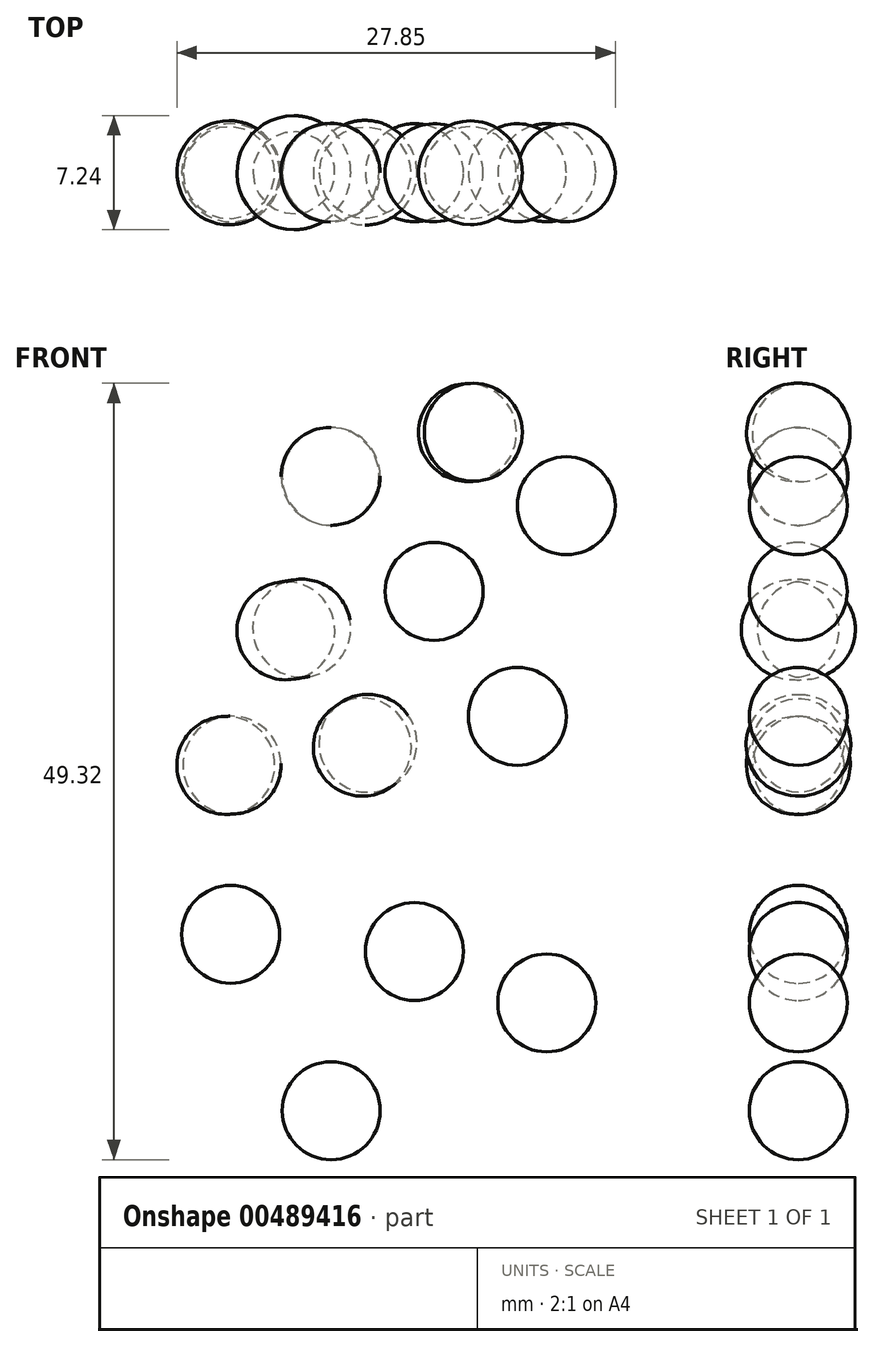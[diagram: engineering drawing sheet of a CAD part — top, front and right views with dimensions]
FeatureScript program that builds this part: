
annotation { "Feature Type Name" : "Feature", "Feature Type Description" : "" }
export const myFeature = defineFeature(function(context is Context, id is Id, definition is map)
    precondition{}
    {
        {
            var Q0;
            Q0=qCreatedBy(makeId("Front.planeOp"),FACE);
            var sketch = newSketch(context, id + "F0", { "sketchPlane" : qUnion([Q0])});
            skCircle(sketch, "E0", {"center": v(-19.54, 6.69) * mm, "radius": 3.11 * mm});
            skCircle(sketch, "E1", {"center": v(-10.05, 8.4) * mm, "radius": 3.11 * mm});
            skCircle(sketch, "E2", {"center": v(-16.58, -6.54) * mm, "radius": 3.11 * mm});
            skCircle(sketch, "E3", {"center": v(-15.34, 16.33) * mm, "radius": 3.11 * mm});
            skCircle(sketch, "E4", {"center": v(-12.85, 26.45) * mm, "radius": 3.11 * mm});
            skCircle(sketch, "E5", {"center": v(-6.94, 21.78) * mm, "radius": 3.11 * mm});
            skCircle(sketch, "E6", {"center": v(-21.87, 23.64) * mm, "radius": 3.11 * mm});
            skCircle(sketch, "E7", {"center": v(-23.74, 14) * mm, "radius": 3.11 * mm});
            skCircle(sketch, "E8", {"center": v(-28.56, 5.29) * mm, "radius": 3.11 * mm});
            skCircle(sketch, "E9", {"center": v(-28.25, -5.45) * mm, "radius": 3.11 * mm});
            skCircle(sketch, "E10", {"center": v(-21.87, -16.65) * mm, "radius": 3.11 * mm});
            skCircle(sketch, "E11", {"center": v(-8.18, -9.8) * mm, "radius": 3.11 * mm});
            skLineSegment(sketch, "E12", {"start": v(-21.95, 30.73) * mm, "end": v(-21.87, 18.16) * mm});
            skLineSegment(sketch, "E13", {"start": v(-24.94, 18.16) * mm, "end": v(-23.74, 10.89) * mm});
            skLineSegment(sketch, "E14", {"start": v(-23.74, 10.89) * mm, "end": v(-22.35, 10.38) * mm});
            skLineSegment(sketch, "E15", {"start": v(-22.35, 10.38) * mm, "end": v(-16.56, 2) * mm});
            skLineSegment(sketch, "E16", {"start": v(-13.37, 32.32) * mm, "end": v(-12.85, 23.33) * mm});
            skLineSegment(sketch, "E17", {"start": v(-6.94, 26.45) * mm, "end": v(-6.94, 18.67) * mm});
            skLineSegment(sketch, "E18", {"start": v(-6.94, 18.67) * mm, "end": v(-6.39, 17.56) * mm});
            skLineSegment(sketch, "E19", {"start": v(-15.34, 21.78) * mm, "end": v(-15.34, 10.38) * mm});
            skLineSegment(sketch, "E20", {"start": v(-10.05, 14) * mm, "end": v(-10.05, 5.29) * mm});
            skLineSegment(sketch, "E21", {"start": v(-10.05, 5.29) * mm, "end": v(-9.18, 4.2) * mm});
            skLineSegment(sketch, "E22", {"start": v(-8.18, -2.4) * mm, "end": v(-8.18, -15.16) * mm});
            skLineSegment(sketch, "E23", {"start": v(-8.18, -15.16) * mm, "end": v(-9.18, -15.16) * mm});
            skLineSegment(sketch, "E24", {"start": v(-16.58, 0) * mm, "end": v(-16.58, -11.97) * mm});
            skLineSegment(sketch, "E25", {"start": v(-16.58, -11.97) * mm, "end": v(-17.76, -11.97) * mm});
            skLineSegment(sketch, "E26", {"start": v(-21.87, -9.8) * mm, "end": v(-21.87, -26.05) * mm});
            skLineSegment(sketch, "E27", {"start": v(-21.87, -26.05) * mm, "end": v(-23.05, -26.05) * mm});
            skLineSegment(sketch, "E28", {"start": v(-28.25, 2) * mm, "end": v(-28.25, -11.56) * mm});
            skLineSegment(sketch, "E29", {"start": v(-28.56, 10.89) * mm, "end": v(-28.25, 2) * mm});
            skSolve(sketch);
        }
        {
            var Q0;
            {var subQ0=sQuery(id+"F0.wireOp",EDGE,"E13");var subQ1=sQuery(id+"F0.wireOp",EDGE,"E7");var subQ2=makeQuery(id+"F0.imprint","INTERSECT",VERTEX,{"disambiguationData":[OD(0.0)],"derivedFrom":[subQ1,subQ0]});Q0=makeQuery(id+"F0.imprint","IMPRINT",FACE,{"disambiguationData":[TD([[makeQuery(id+"F0.imprint","IMPRINT",EDGE,{"disambiguationData":[TD([[subQ2,-1.0]])],"derivedFrom":subQ1}),1.0]])]});}
            var Q1;
            Q1=sQuery(id+"F0.wireOp",EDGE,"E13");
            revolve(context, id + "F1", {"entities" : qUnion([Q0]), "axis" : qUnion([Q1]), "revolveType" : RevolveType.FULL});
        }
        {
            var Q0;
            {var subQ0=sQuery(id+"F0.wireOp",EDGE,"E12");var subQ1=sQuery(id+"F0.wireOp",EDGE,"E6");var subQ2=makeQuery(id+"F0.imprint","INTERSECT",VERTEX,{"disambiguationData":[OD(0.0)],"derivedFrom":[subQ1,subQ0]});Q0=makeQuery(id+"F0.imprint","IMPRINT",FACE,{"disambiguationData":[TD([[makeQuery(id+"F0.imprint","IMPRINT",EDGE,{"disambiguationData":[TD([[subQ2,-1.0]])],"derivedFrom":subQ1}),1.0]])]});}
            var Q1;
            Q1=sQuery(id+"F0.wireOp",EDGE,"E12");
            revolve(context, id + "F2", {"entities" : qUnion([Q0]), "axis" : qUnion([Q1]), "revolveType" : RevolveType.FULL});
        }
        {
            var Q0;
            {var subQ0=sQuery(id+"F0.wireOp",EDGE,"E16");var subQ1=sQuery(id+"F0.wireOp",EDGE,"E4");var subQ2=makeQuery(id+"F0.imprint","INTERSECT",VERTEX,{"disambiguationData":[OD(0.0)],"derivedFrom":[subQ1,subQ0]});Q0=makeQuery(id+"F0.imprint","IMPRINT",FACE,{"disambiguationData":[TD([[makeQuery(id+"F0.imprint","IMPRINT",EDGE,{"disambiguationData":[TD([[subQ2,-1.0]])],"derivedFrom":subQ1}),1.0]])]});}
            var Q1;
            Q1=sQuery(id+"F0.wireOp",EDGE,"E16");
            revolve(context, id + "F3", {"entities" : qUnion([Q0]), "axis" : qUnion([Q1]), "revolveType" : RevolveType.FULL});
        }
        {
            var Q0;
            {var subQ0=sQuery(id+"F0.wireOp",EDGE,"E17");var subQ1=sQuery(id+"F0.wireOp",EDGE,"E5");var subQ2=makeQuery(id+"F0.imprint","INTERSECT",VERTEX,{"disambiguationData":[OD(0.0)],"derivedFrom":[subQ1,subQ0]});Q0=makeQuery(id+"F0.imprint","IMPRINT",FACE,{"disambiguationData":[TD([[makeQuery(id+"F0.imprint","IMPRINT",EDGE,{"disambiguationData":[TD([[subQ2,-1.0]])],"derivedFrom":subQ1}),1.0]])]});}
            var Q1;
            Q1=sQuery(id+"F0.wireOp",EDGE,"E17");
            revolve(context, id + "F4", {"entities" : qUnion([Q0]), "axis" : qUnion([Q1]), "revolveType" : RevolveType.FULL});
        }
        {
            var Q0;
            {var subQ0=sQuery(id+"F0.wireOp",EDGE,"E29");var subQ1=sQuery(id+"F0.wireOp",EDGE,"E8");var subQ2=makeQuery(id+"F0.imprint","INTERSECT",VERTEX,{"disambiguationData":[OD(0.0)],"derivedFrom":[subQ1,subQ0]});Q0=makeQuery(id+"F0.imprint","IMPRINT",FACE,{"disambiguationData":[TD([[makeQuery(id+"F0.imprint","IMPRINT",EDGE,{"disambiguationData":[TD([[subQ2,-1.0]])],"derivedFrom":subQ1}),1.0]])]});}
            var Q1;
            Q1=sQuery(id+"F0.wireOp",EDGE,"E29");
            revolve(context, id + "F5", {"entities" : qUnion([Q0]), "axis" : qUnion([Q1]), "revolveType" : RevolveType.FULL});
        }
        {
            var Q0;
            {var subQ0=sQuery(id+"F0.wireOp",EDGE,"E15");var subQ1=sQuery(id+"F0.wireOp",EDGE,"E0");var subQ2=makeQuery(id+"F0.imprint","INTERSECT",VERTEX,{"disambiguationData":[OD(0.0)],"derivedFrom":[subQ1,subQ0]});Q0=makeQuery(id+"F0.imprint","IMPRINT",FACE,{"disambiguationData":[TD([[makeQuery(id+"F0.imprint","IMPRINT",EDGE,{"disambiguationData":[TD([[subQ2,1.0]])],"derivedFrom":subQ1}),1.0]])]});}
            var Q1;
            Q1=sQuery(id+"F0.wireOp",EDGE,"E15");
            revolve(context, id + "F6", {"entities" : qUnion([Q0]), "axis" : qUnion([Q1]), "revolveType" : RevolveType.FULL});
        }
        {
            var Q0;
            {var subQ0=sQuery(id+"F0.wireOp",EDGE,"E19");var subQ1=sQuery(id+"F0.wireOp",EDGE,"E3");var subQ2=makeQuery(id+"F0.imprint","INTERSECT",VERTEX,{"disambiguationData":[OD(0.0)],"derivedFrom":[subQ1,subQ0]});Q0=makeQuery(id+"F0.imprint","IMPRINT",FACE,{"disambiguationData":[TD([[makeQuery(id+"F0.imprint","IMPRINT",EDGE,{"disambiguationData":[TD([[subQ2,-1.0]])],"derivedFrom":subQ1}),1.0]])]});}
            var Q1;
            Q1=sQuery(id+"F0.wireOp",EDGE,"E19");
            revolve(context, id + "F7", {"entities" : qUnion([Q0]), "axis" : qUnion([Q1]), "revolveType" : RevolveType.FULL});
        }
        {
            var Q0;
            {var subQ0=sQuery(id+"F0.wireOp",EDGE,"E20");var subQ1=sQuery(id+"F0.wireOp",EDGE,"E1");var subQ2=makeQuery(id+"F0.imprint","INTERSECT",VERTEX,{"disambiguationData":[OD(0.0)],"derivedFrom":[subQ1,subQ0]});Q0=makeQuery(id+"F0.imprint","IMPRINT",FACE,{"disambiguationData":[TD([[makeQuery(id+"F0.imprint","IMPRINT",EDGE,{"disambiguationData":[TD([[subQ2,-1.0]])],"derivedFrom":subQ1}),1.0]])]});}
            var Q1;
            Q1=sQuery(id+"F0.wireOp",EDGE,"E20");
            revolve(context, id + "F8", {"entities" : qUnion([Q0]), "axis" : qUnion([Q1]), "revolveType" : RevolveType.FULL});
        }
        {
            var Q0;
            {var subQ0=sQuery(id+"F0.wireOp",EDGE,"E28");var subQ1=sQuery(id+"F0.wireOp",EDGE,"E9");var subQ2=makeQuery(id+"F0.imprint","INTERSECT",VERTEX,{"disambiguationData":[OD(0.0)],"derivedFrom":[subQ1,subQ0]});Q0=makeQuery(id+"F0.imprint","IMPRINT",FACE,{"disambiguationData":[TD([[makeQuery(id+"F0.imprint","IMPRINT",EDGE,{"disambiguationData":[TD([[subQ2,-1.0]])],"derivedFrom":subQ1}),1.0]])]});}
            var Q1;
            Q1=sQuery(id+"F0.wireOp",EDGE,"E28");
            revolve(context, id + "F9", {"entities" : qUnion([Q0]), "axis" : qUnion([Q1]), "revolveType" : RevolveType.FULL});
        }
        {
            var Q0;
            {var subQ0=sQuery(id+"F0.wireOp",EDGE,"E26");var subQ1=sQuery(id+"F0.wireOp",EDGE,"E10");var subQ2=makeQuery(id+"F0.imprint","INTERSECT",VERTEX,{"disambiguationData":[OD(0.0)],"derivedFrom":[subQ1,subQ0]});Q0=makeQuery(id+"F0.imprint","IMPRINT",FACE,{"disambiguationData":[TD([[makeQuery(id+"F0.imprint","IMPRINT",EDGE,{"disambiguationData":[TD([[subQ2,-1.0]])],"derivedFrom":subQ1}),1.0]])]});}
            var Q1;
            Q1=sQuery(id+"F0.wireOp",EDGE,"E26");
            revolve(context, id + "F10", {"entities" : qUnion([Q0]), "axis" : qUnion([Q1]), "revolveType" : RevolveType.FULL});
        }
        {
            var Q0;
            {var subQ0=sQuery(id+"F0.wireOp",EDGE,"E24");var subQ1=sQuery(id+"F0.wireOp",EDGE,"E2");var subQ2=makeQuery(id+"F0.imprint","INTERSECT",VERTEX,{"disambiguationData":[OD(0.0)],"derivedFrom":[subQ1,subQ0]});Q0=makeQuery(id+"F0.imprint","IMPRINT",FACE,{"disambiguationData":[TD([[makeQuery(id+"F0.imprint","IMPRINT",EDGE,{"disambiguationData":[TD([[subQ2,-1.0]])],"derivedFrom":subQ1}),1.0]])]});}
            var Q1;
            Q1=sQuery(id+"F0.wireOp",EDGE,"E24");
            revolve(context, id + "F11", {"entities" : qUnion([Q0]), "axis" : qUnion([Q1]), "revolveType" : RevolveType.FULL});
        }
        {
            var Q0;
            {var subQ0=sQuery(id+"F0.wireOp",EDGE,"E22");var subQ1=sQuery(id+"F0.wireOp",EDGE,"E11");var subQ2=makeQuery(id+"F0.imprint","INTERSECT",VERTEX,{"disambiguationData":[OD(0.0)],"derivedFrom":[subQ1,subQ0]});Q0=makeQuery(id+"F0.imprint","IMPRINT",FACE,{"disambiguationData":[TD([[makeQuery(id+"F0.imprint","IMPRINT",EDGE,{"disambiguationData":[TD([[subQ2,-1.0]])],"derivedFrom":subQ1}),1.0]])]});}
            var Q1;
            Q1=sQuery(id+"F0.wireOp",EDGE,"E22");
            revolve(context, id + "F12", {"entities" : qUnion([Q0]), "axis" : qUnion([Q1]), "revolveType" : RevolveType.FULL});
        }
    });
